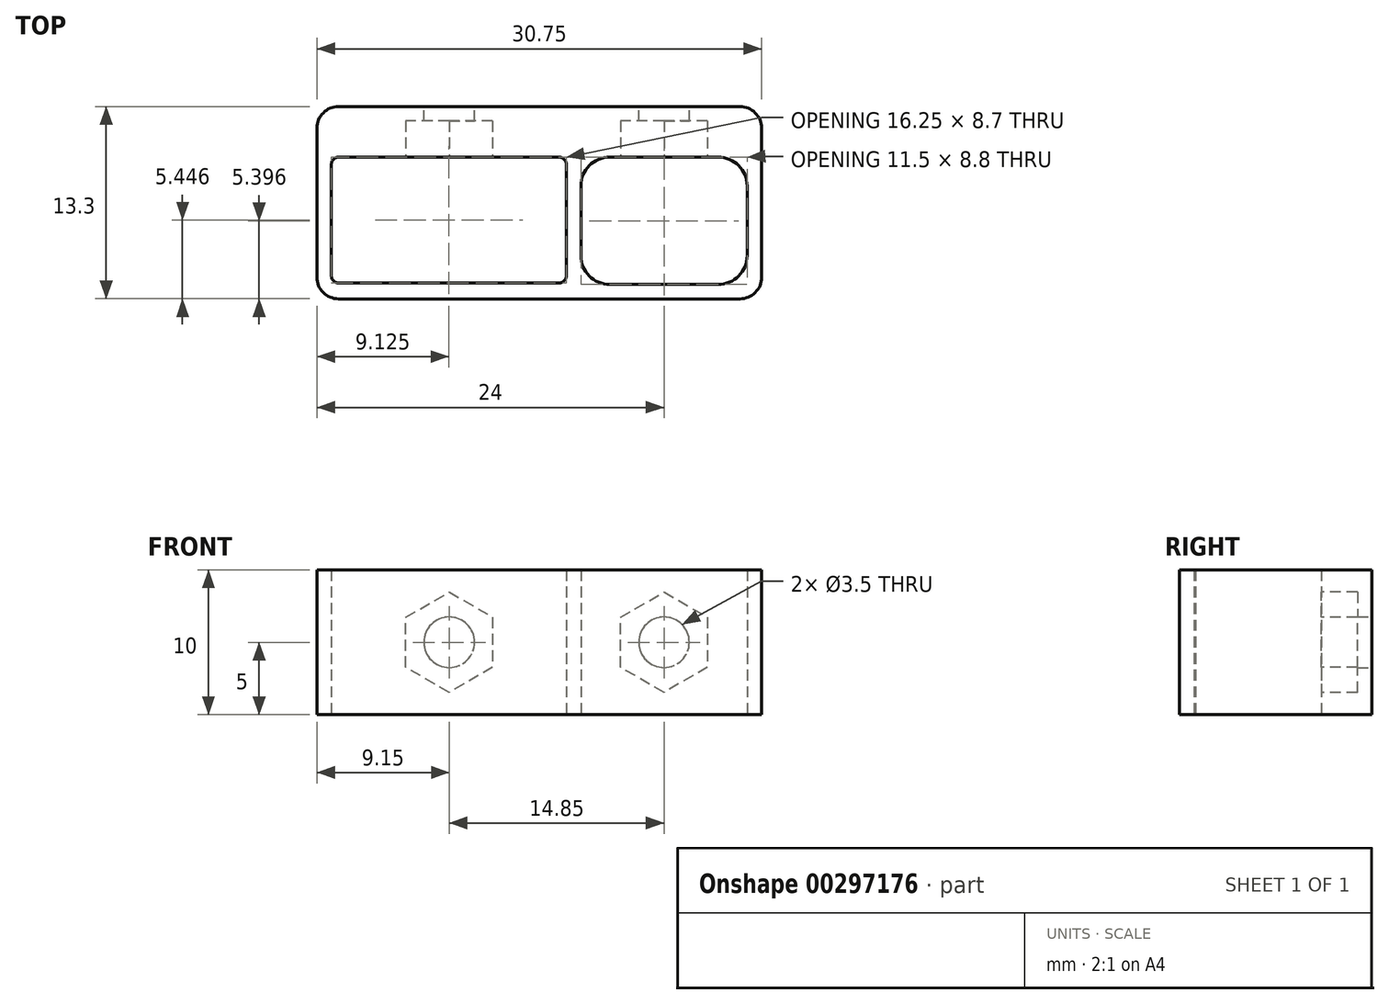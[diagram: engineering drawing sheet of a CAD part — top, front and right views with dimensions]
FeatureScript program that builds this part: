
annotation { "Feature Type Name" : "Feature", "Feature Type Description" : "" }
export const myFeature = defineFeature(function(context is Context, id is Id, definition is map)
    precondition{}
    {
        {
            var Q0;
            Q0=qCreatedBy(makeId("Top.planeOp"),FACE);
            var sketch = newSketch(context, id + "F0", { "sketchPlane" : qUnion([Q0])});
            skLineSegment(sketch, "E0.bottom", {"start": v(-29.89, -2.24) * mm, "end": v(0.86, -2.24) * mm});
            skLineSegment(sketch, "E0.top", {"start": v(-29.89, -15.54) * mm, "end": v(0.86, -15.54) * mm});
            skLineSegment(sketch, "E0.left", {"start": v(-29.89, -2.24) * mm, "end": v(-29.89, -15.54) * mm});
            skLineSegment(sketch, "E1.bottom", {"start": v(-28.89, -5.74) * mm, "end": v(-12.64, -5.74) * mm});
            skLineSegment(sketch, "E1.top", {"start": v(-28.89, -14.44) * mm, "end": v(-12.64, -14.44) * mm});
            skLineSegment(sketch, "E1.left", {"start": v(-28.89, -5.74) * mm, "end": v(-28.89, -14.44) * mm});
            skLineSegment(sketch, "E2.bottom", {"start": v(-11.64, -5.74) * mm, "end": v(-0.14, -5.74) * mm});
            skLineSegment(sketch, "E2.top", {"start": v(-11.64, -14.54) * mm, "end": v(-0.14, -14.54) * mm});
            skLineSegment(sketch, "E3", {"start": v(-12.64, -5.74) * mm, "end": v(-12.64, -14.44) * mm});
            skLineSegment(sketch, "E4", {"start": v(-11.64, -14.54) * mm, "end": v(-11.64, -5.74) * mm});
            skLineSegment(sketch, "E5", {"start": v(-0.14, -5.74) * mm, "end": v(-0.14, -14.54) * mm});
            skLineSegment(sketch, "E6", {"start": v(0.86, -2.24) * mm, "end": v(0.86, -15.54) * mm});
            skSolve(sketch);
        }
        {
            var Q0;
            Q0=makeQuery(id+"F0.imprint","IMPRINT",FACE,{"disambiguationData":[TD([[makeQuery(id+"F0.imprint","IMPRINT",EDGE,{"derivedFrom":sQuery(id+"F0.wireOp",EDGE,"E0.bottom")}),-1.0]])]});
            extrude(context, id + "F1", {"entities" : qUnion([Q0]), "depth" : 10 * mm});
        }
        {
            var Q0;
            Q0=makeQuery(id+"F1.opExtrude","SWEPT_EDGE",EDGE,{"disambiguationData":[OSD([sQuery(id+"F0.wireOp",EDGE,"E1.bottom"),sQuery(id+"F0.wireOp",EDGE,"E1.left")])]});
            var Q1;
            Q1=makeQuery(id+"F1.opExtrude","SWEPT_EDGE",EDGE,{"disambiguationData":[OSD([sQuery(id+"F0.wireOp",EDGE,"E1.bottom"),sQuery(id+"F0.wireOp",EDGE,"E1.right")])]});
            var Q2;
            Q2=makeQuery(id+"F1.opExtrude","SWEPT_EDGE",EDGE,{"disambiguationData":[OSD([sQuery(id+"F0.wireOp",EDGE,"E1.top"),sQuery(id+"F0.wireOp",EDGE,"E1.left")])]});
            var Q3;
            Q3=makeQuery(id+"F1.opExtrude","SWEPT_EDGE",EDGE,{"disambiguationData":[OSD([sQuery(id+"F0.wireOp",EDGE,"E1.top"),sQuery(id+"F0.wireOp",EDGE,"E1.right")])]});
            fillet(context, id + "F2", {"entities" : qUnion([Q0, Q1, Q2, Q3]), "radius" : 0.5 * mm, "tangentPropagation" : true, "allowEdgeOverflow" : false});
        }
        {
            var Q0;
            Q0=makeQuery(id+"F1.opExtrude","SWEPT_EDGE",EDGE,{"disambiguationData":[OSD([sQuery(id+"F0.wireOp",EDGE,"E2.top"),sQuery(id+"F0.wireOp",EDGE,"E2.right")])]});
            var Q1;
            Q1=makeQuery(id+"F1.opExtrude","SWEPT_EDGE",EDGE,{"disambiguationData":[OSD([sQuery(id+"F0.wireOp",EDGE,"E2.top"),sQuery(id+"F0.wireOp",EDGE,"E2.left")])]});
            var Q2;
            Q2=makeQuery(id+"F1.opExtrude","SWEPT_EDGE",EDGE,{"disambiguationData":[OSD([sQuery(id+"F0.wireOp",EDGE,"E2.bottom"),sQuery(id+"F0.wireOp",EDGE,"E2.left")])]});
            var Q3;
            Q3=makeQuery(id+"F1.opExtrude","SWEPT_EDGE",EDGE,{"disambiguationData":[OSD([sQuery(id+"F0.wireOp",EDGE,"E2.bottom"),sQuery(id+"F0.wireOp",EDGE,"E2.right")])]});
            fillet(context, id + "F3", {"entities" : qUnion([Q0, Q1, Q2, Q3]), "radius" : 2 * mm, "tangentPropagation" : true, "allowEdgeOverflow" : false});
        }
        {
            var Q0;
            Q0=makeQuery(id+"F1.opExtrude","SWEPT_EDGE",EDGE,{"disambiguationData":[OSD([sQuery(id+"F0.wireOp",EDGE,"E0.top"),sQuery(id+"F0.wireOp",EDGE,"E0.left")])]});
            var Q1;
            Q1=makeQuery(id+"F1.opExtrude","SWEPT_EDGE",EDGE,{"disambiguationData":[OSD([sQuery(id+"F0.wireOp",EDGE,"E0.bottom"),sQuery(id+"F0.wireOp",EDGE,"E0.left")])]});
            var Q2;
            Q2=makeQuery(id+"F1.opExtrude","SWEPT_EDGE",EDGE,{"disambiguationData":[OSD([sQuery(id+"F0.wireOp",EDGE,"E0.top"),sQuery(id+"F0.wireOp",EDGE,"E0.right")])]});
            var Q3;
            Q3=makeQuery(id+"F1.opExtrude","SWEPT_EDGE",EDGE,{"disambiguationData":[OSD([sQuery(id+"F0.wireOp",EDGE,"E0.bottom"),sQuery(id+"F0.wireOp",EDGE,"E0.right")])]});
            fillet(context, id + "F4", {"entities" : qUnion([Q0, Q1, Q2, Q3]), "radius" : 1.5 * mm, "tangentPropagation" : true, "allowEdgeOverflow" : false});
        }
        {
            var Q0;
            Q0=makeQuery(id+"F1.opExtrude","SWEPT_FACE",FACE,{"disambiguationData":[OSD([sQuery(id+"F0.wireOp",EDGE,"E0.bottom")])]});
            var sketch = newSketch(context, id + "F5", { "sketchPlane" : qUnion([Q0])});
            skCircle(sketch, "E7.cCircle", {"center": v(20.74, 5) * mm, "radius": 2.75 * mm, "construction": true});
            skLineSegment(sketch, "E7.0", {"start": v(17.99, 3.41) * mm, "end": v(17.99, 6.59) * mm});
            skLineSegment(sketch, "E7.1", {"start": v(17.99, 6.59) * mm, "end": v(20.74, 8.18) * mm});
            skLineSegment(sketch, "E7.2", {"start": v(20.74, 8.18) * mm, "end": v(23.49, 6.59) * mm});
            skLineSegment(sketch, "E7.3", {"start": v(23.49, 6.59) * mm, "end": v(23.49, 3.41) * mm});
            skLineSegment(sketch, "E7.4", {"start": v(23.49, 3.41) * mm, "end": v(20.74, 1.82) * mm});
            skLineSegment(sketch, "E7.5", {"start": v(20.74, 1.82) * mm, "end": v(17.99, 3.41) * mm});
            skPoint(sketch, "E7.0.midPoint", {"position": v(17.99, 5) * mm});
            skCircle(sketch, "E8.cCircle", {"center": v(5.89, 5) * mm, "radius": 2.75 * mm, "construction": true});
            skLineSegment(sketch, "E8.0", {"start": v(3.14, 3.41) * mm, "end": v(3.14, 6.59) * mm});
            skLineSegment(sketch, "E8.1", {"start": v(3.14, 6.59) * mm, "end": v(5.89, 8.18) * mm});
            skLineSegment(sketch, "E8.2", {"start": v(5.89, 8.18) * mm, "end": v(8.64, 6.59) * mm});
            skLineSegment(sketch, "E8.3", {"start": v(8.64, 6.59) * mm, "end": v(8.64, 3.41) * mm});
            skLineSegment(sketch, "E8.4", {"start": v(8.64, 3.41) * mm, "end": v(5.89, 1.82) * mm});
            skLineSegment(sketch, "E8.5", {"start": v(5.89, 1.82) * mm, "end": v(3.14, 3.41) * mm});
            skPoint(sketch, "E8.0.midPoint", {"position": v(3.14, 5) * mm});
            skCircle(sketch, "E9", {"center": v(5.89, 5) * mm, "radius": 1.75 * mm});
            skCircle(sketch, "E10", {"center": v(20.74, 5) * mm, "radius": 1.75 * mm});
            skSolve(sketch);
        }
        {
            var Q0;
            Q0=makeQuery(id+"F1.opExtrude","SWEPT_FACE",FACE,{"disambiguationData":[OSD([sQuery(id+"F0.wireOp",EDGE,"E2.bottom")])]});
            var sketch = newSketch(context, id + "F6", { "sketchPlane" : qUnion([Q0])});
            skCircle(sketch, "E11.cCircle", {"center": v(-20.74, 5) * mm, "radius": 3 * mm, "construction": true});
            skLineSegment(sketch, "E11.0", {"start": v(-23.74, 3.27) * mm, "end": v(-23.74, 6.73) * mm});
            skLineSegment(sketch, "E11.1", {"start": v(-23.74, 6.73) * mm, "end": v(-20.74, 8.46) * mm});
            skLineSegment(sketch, "E11.2", {"start": v(-20.74, 8.46) * mm, "end": v(-17.74, 6.73) * mm});
            skLineSegment(sketch, "E11.3", {"start": v(-17.74, 6.73) * mm, "end": v(-17.74, 3.27) * mm});
            skLineSegment(sketch, "E11.4", {"start": v(-17.74, 3.27) * mm, "end": v(-20.74, 1.54) * mm});
            skLineSegment(sketch, "E11.5", {"start": v(-20.74, 1.54) * mm, "end": v(-23.74, 3.27) * mm});
            skPoint(sketch, "E11.0.midPoint", {"position": v(-23.74, 5) * mm});
            skCircle(sketch, "E12.cCircle", {"center": v(-5.89, 5) * mm, "radius": 3 * mm, "construction": true});
            skLineSegment(sketch, "E12.0", {"start": v(-8.89, 3.27) * mm, "end": v(-8.89, 6.73) * mm});
            skLineSegment(sketch, "E12.1", {"start": v(-8.89, 6.73) * mm, "end": v(-5.89, 8.46) * mm});
            skLineSegment(sketch, "E12.2", {"start": v(-5.89, 8.46) * mm, "end": v(-2.89, 6.73) * mm});
            skLineSegment(sketch, "E12.3", {"start": v(-2.89, 6.73) * mm, "end": v(-2.89, 3.27) * mm});
            skLineSegment(sketch, "E12.4", {"start": v(-2.89, 3.27) * mm, "end": v(-5.89, 1.54) * mm});
            skLineSegment(sketch, "E12.5", {"start": v(-5.89, 1.54) * mm, "end": v(-8.89, 3.27) * mm});
            skPoint(sketch, "E12.0.midPoint", {"position": v(-8.89, 5) * mm});
            skSolve(sketch);
        }
        {
            var Q0;
            Q0=makeQuery(id+"F6.imprint","IMPRINT",FACE,{"disambiguationData":[TD([[makeQuery(id+"F6.imprint","IMPRINT",EDGE,{"derivedFrom":sQuery(id+"F6.wireOp",EDGE,"E12.0")}),-1.0]])]});
            var Q1;
            Q1=makeQuery(id+"F6.imprint","IMPRINT",FACE,{"disambiguationData":[TD([[makeQuery(id+"F6.imprint","IMPRINT",EDGE,{"derivedFrom":sQuery(id+"F6.wireOp",EDGE,"E11.0")}),-1.0]])]});
            extrude(context, id + "F7", {"entities" : qUnion([Q0, Q1]), "operationType" : NewBodyOperationType.REMOVE, "oppositeDirection" : true, "depth" : 2.5 * mm});
        }
        {
            var Q0;
            Q0=makeQuery(id+"F5.imprint","IMPRINT",FACE,{"disambiguationData":[TD([[makeQuery(id+"F5.imprint","IMPRINT",EDGE,{"derivedFrom":sQuery(id+"F5.wireOp",EDGE,"E9")}),1.0]])]});
            var Q1;
            Q1=makeQuery(id+"F5.imprint","IMPRINT",FACE,{"disambiguationData":[TD([[makeQuery(id+"F5.imprint","IMPRINT",EDGE,{"derivedFrom":sQuery(id+"F5.wireOp",EDGE,"E10")}),1.0]])]});
            extrude(context, id + "F8", {"entities" : qUnion([Q0, Q1]), "operationType" : NewBodyOperationType.REMOVE, "oppositeDirection" : true, "depth" : 8 * mm});
        }
    });
